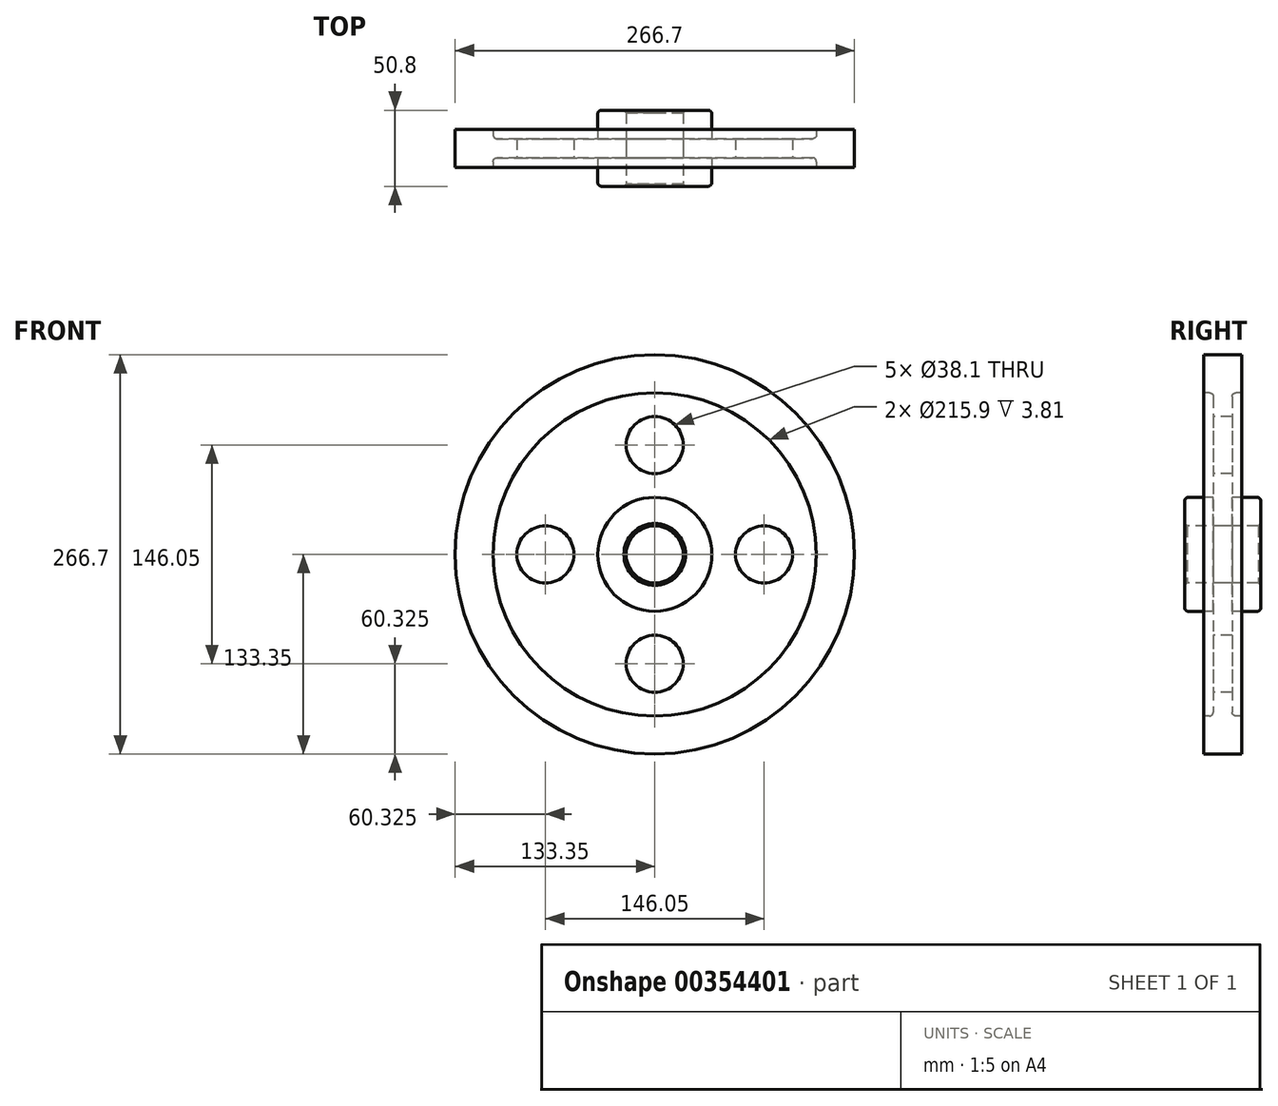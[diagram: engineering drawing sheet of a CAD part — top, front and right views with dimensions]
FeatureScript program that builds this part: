
annotation { "Feature Type Name" : "Feature", "Feature Type Description" : "" }
export const myFeature = defineFeature(function(context is Context, id is Id, definition is map)
    precondition{}
    {
        {
            var Q0;
            Q0=qCreatedBy(makeId("Right.planeOp"),FACE);
            var sketch = newSketch(context, id + "F0", { "sketchPlane" : qUnion([Q0])});
            skLineSegment(sketch, "E0", {"start": v(0, 0) * mm, "end": v(76.2, 0) * mm, "construction": true});
            skLineSegment(sketch, "E1.0", {"start": v(0, 19.05) * mm, "end": v(25.4, 19.05) * mm});
            skLineSegment(sketch, "E2.0", {"start": v(6.35, 38.1) * mm, "end": v(25.4, 38.1) * mm});
            skLineSegment(sketch, "E3.0", {"start": v(6.35, 107.95) * mm, "end": v(12.7, 107.95) * mm});
            skLineSegment(sketch, "E4.0", {"start": v(0, 133.35) * mm, "end": v(12.7, 133.35) * mm});
            skLineSegment(sketch, "E5", {"start": v(0, 133.35) * mm, "end": v(0, 0) * mm, "construction": true});
            skLineSegment(sketch, "E6.0", {"start": v(25.4, 38.1) * mm, "end": v(25.4, 19.05) * mm});
            skLineSegment(sketch, "E7.0", {"start": v(12.7, 133.35) * mm, "end": v(12.7, 107.95) * mm});
            skLineSegment(sketch, "E8.0", {"start": v(6.35, 107.95) * mm, "end": v(6.35, 38.1) * mm});
            skLineSegment(sketch, "E9.MirrorCS", {"start": v(-12.7, 133.35) * mm, "end": v(-12.7, 107.95) * mm});
            skLineSegment(sketch, "E10.MirrorCS", {"start": v(-6.35, 107.95) * mm, "end": v(-6.35, 38.1) * mm});
            skLineSegment(sketch, "E11.MirrorCS", {"start": v(-6.35, 38.1) * mm, "end": v(-25.4, 38.1) * mm});
            skLineSegment(sketch, "E12.MirrorCS", {"start": v(-25.4, 38.1) * mm, "end": v(-25.4, 19.05) * mm});
            skLineSegment(sketch, "E13.MirrorCS", {"start": v(-6.35, 107.95) * mm, "end": v(-12.7, 107.95) * mm});
            skLineSegment(sketch, "E14.MirrorCS", {"start": v(0, -95.25) * mm, "end": v(12.7, -95.25) * mm});
            skLineSegment(sketch, "E15.MirrorCS", {"start": v(0, 247.65) * mm, "end": v(25.4, 247.65) * mm});
            skLineSegment(sketch, "E16.MirrorCS", {"start": v(0, 133.35) * mm, "end": v(-12.7, 133.35) * mm});
            skLineSegment(sketch, "E17.MirrorCS", {"start": v(0, 19.05) * mm, "end": v(-25.4, 19.05) * mm});
            skSolve(sketch);
        }
        {
            var Q0;
            Q0=makeQuery(id+"F0.imprint","IMPRINT",FACE,{"disambiguationData":[TD([[makeQuery(id+"F0.imprint","IMPRINT",EDGE,{"derivedFrom":sQuery(id+"F0.wireOp",EDGE,"E1.0")}),1.0]])]});
            var Q1;
            Q1=sQuery(id+"F0.wireOp",EDGE,"E0");
            revolve(context, id + "F1", {"entities" : qUnion([Q0]), "axis" : qUnion([Q1]), "revolveType" : RevolveType.FULL});
        }
        {
            var Q0;
            Q0=makeQuery(id+"F1.opRevolve","SWEPT_FACE",FACE,{"disambiguationData":[OSD([sQuery(id+"F0.wireOp",EDGE,"E10.MirrorCS")])]});
            cPlane(context, id + "F2", {"entities" : qUnion([Q0]), "cplaneType" : CPlaneType.OFFSET, "offset" : 25.4 * mm, "width" : 152.4 * mm, "height" : 152.4 * mm});
        }
        {
            var Q0;
            Q0=qCreatedBy(id+"F2.planeOp",FACE);
            var sketch = newSketch(context, id + "F3", { "sketchPlane" : qUnion([Q0])});
            skLineSegment(sketch, "E18", {"start": v(0, 0) * mm, "end": v(0, 73.03) * mm});
            skCircle(sketch, "E19", {"center": v(0, 73.03) * mm, "radius": 19.05 * mm});
            skCircle(sketch, "E20.1.0", {"center": v(-73.03, 0) * mm, "radius": 19.05 * mm});
            skCircle(sketch, "E20.2.0", {"center": v(0, -73.03) * mm, "radius": 19.05 * mm});
            skCircle(sketch, "E20.3.0", {"center": v(73.03, 0) * mm, "radius": 19.05 * mm});
            skPoint(sketch, "E20.center", {"position": v(0, 0) * mm});
            skSolve(sketch);
        }
        {
            var Q0;
            Q0=makeQuery(id+"F3.imprint","IMPRINT",FACE,{"disambiguationData":[TD([[makeQuery(id+"F3.imprint","IMPRINT",EDGE,{"derivedFrom":sQuery(id+"F3.wireOp",EDGE,"E20.1.0")}),1.0]])]});
            var Q1;
            Q1=makeQuery(id+"F3.imprint","IMPRINT",FACE,{"disambiguationData":[TD([[makeQuery(id+"F3.imprint","IMPRINT",EDGE,{"derivedFrom":sQuery(id+"F3.wireOp",EDGE,"E20.2.0")}),1.0]])]});
            var Q2;
            Q2=makeQuery(id+"F3.imprint","IMPRINT",FACE,{"disambiguationData":[TD([[makeQuery(id+"F3.imprint","IMPRINT",EDGE,{"derivedFrom":sQuery(id+"F3.wireOp",EDGE,"E20.3.0")}),1.0]])]});
            var Q3;
            Q3=makeQuery(id+"F3.imprint","IMPRINT",FACE,{"disambiguationData":[TD([[makeQuery(id+"F3.imprint","IMPRINT",EDGE,{"derivedFrom":sQuery(id+"F3.wireOp",EDGE,"E19")}),1.0]])]});
            extrude(context, id + "F4", {"entities" : qUnion([Q0, Q1, Q2, Q3]), "operationType" : NewBodyOperationType.REMOVE, "oppositeDirection" : true, "depth" : 50.8 * mm});
        }
        {
            var Q0;
            Q0=makeQuery(id+"F1.opRevolve","SWEPT_EDGE",EDGE,{"disambiguationData":[OSD([sQuery(id+"F0.wireOp",EDGE,"E10.MirrorCS"),sQuery(id+"F0.wireOp",EDGE,"E13.MirrorCS")])]});
            var Q1;
            Q1=makeQuery(id+"F1.opRevolve","SWEPT_EDGE",EDGE,{"disambiguationData":[OSD([sQuery(id+"F0.wireOp",EDGE,"E11.MirrorCS"),sQuery(id+"F0.wireOp",EDGE,"E12.MirrorCS")])]});
            var Q2;
            Q2=makeQuery(id+"F1.opRevolve","SWEPT_EDGE",EDGE,{"disambiguationData":[OSD([sQuery(id+"F0.wireOp",EDGE,"E3.0"),sQuery(id+"F0.wireOp",EDGE,"E8.0")])]});
            var Q3;
            Q3=makeQuery(id+"F1.opRevolve","SWEPT_EDGE",EDGE,{"disambiguationData":[OSD([sQuery(id+"F0.wireOp",EDGE,"E2.0"),sQuery(id+"F0.wireOp",EDGE,"E6.0")])]});
            fillet(context, id + "F5", {"entities" : qUnion([Q0, Q1, Q2, Q3]), "radius" : 2.54 * mm, "tangentPropagation" : true, "allowEdgeOverflow" : false});
        }
        {
            var Q0;
            Q0=makeQuery(id+"F1.opRevolve","SWEPT_EDGE",EDGE,{"disambiguationData":[OSD([sQuery(id+"F0.wireOp",EDGE,"E12.MirrorCS"),sQuery(id+"F0.wireOp",EDGE,"E17.MirrorCS")])]});
            var Q1;
            Q1=makeQuery(id+"F1.opRevolve","SWEPT_EDGE",EDGE,{"disambiguationData":[OSD([sQuery(id+"F0.wireOp",EDGE,"E1.0"),sQuery(id+"F0.wireOp",EDGE,"E6.0")])]});
            chamfer(context, id + "F6", {"entities" : qUnion([Q0, Q1]), "width" : 1.59 * mm, "tangentPropagation" : true});
        }
    });
